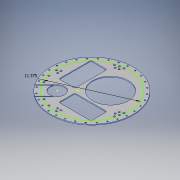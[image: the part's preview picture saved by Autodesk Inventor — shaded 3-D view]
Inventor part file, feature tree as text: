
AUTODESK INVENTOR PART (.ipt)
format: ipt  version: 2018 (Build 220112000, 112)  size: 325,120 bytes
history: native  units: in
note: dims shown in document units (in); Inventor stores cm internally (conversion verified against a paired STEP export)
features: sketch x8, extrude x4, hole x4, pattern_circular x1, fillet x1
ambient origin geometry x8: Origin, YZ Plane, XZ Plane, XY Plane, X Axis, Y Axis, Z Axis, Center Point
bodies: Solid1 (feature_tree)
feature tree (18):
  extrude  "Extrusion1"  TaperAngle=135.0deg  [1 undecoded]
  extrude  "Extrusion2"  Depth=2.25in
  hole  "Hole3"  [1 undecoded]
  pattern_circular  "Circular Pattern1"  [2 undecoded]
  hole  "Hole5"  [1 undecoded]
  hole  "Hole6"  [1 undecoded]
  extrude  "Extrusion3"  Depth=0.25in
  fillet  "Fillet1"  Radius=0.2749in
  sketch  "Sketch15"  dims[d8=12.75in]
  extrude  "Extrusion4"  Depth=0.25in
  hole  "Hole9"  [1 undecoded]
  sketch  "Sketch1"  dims[d0=3.6in d1=135.0deg]
  sketch  "Sketch2"  dims[d2=5.5in d3=2.25in]
  sketch  "Sketch6"  dims[d4=45.0deg d5=2.27in]
  sketch  "Sketch11"  dims[d6=1.56in]
  sketch  "Sketch13"  dims[d7=315.0deg]
  sketch  "Sketch17"  dims[d9=0.125in d10=0.0in]
  sketch  "Sketch19"  dims[d11=0.0in d12=0.0in d65=6.1in d66=0.0344in d67=0.196in d68=0.5in d69=0.375in d70=0.25in d71=0.5635in d72=0.75in d73=0.8108in d74=12.5984in d75=360.0deg d97=8.5in d98=0.2749in d99=8.5in d100=0.3436in d101=9.708in d102=9.708in d103=1.5748in d105=360.0deg d109=7.75in d110=0.962in d111=7.75in d112=0.8933in d116=0.266in d117=0.75in d118=0.507in d119=0.25in d120=0.5635in d121=1.0in d122=0.8108in d132=0.266in d133=0.75in d134=0.507in d135=0.25in d136=0.5635in d137=1.0in d138=0.8108in d147=11.0in d148=9.708in d149=9.708in d150=5.5in d152=5.5in d153=5.5in d154=5.5in d155=5.0in d156=90.0deg d157=2.5in d160=1.0in d161=45.0deg d162=1.0in d163=0.0in d164=2.9in d165=180.0deg d166=1.5in d167=90.0deg d168=0.25in d171=11.375in d180=0.1in d181=0.1in d182=1.0in d183=0.0in d201=10.1in d204=0.266in d205=0.75in d206=0.507in d207=0.25in d208=0.5635in d209=1.0in d210=0.8108in d212=1.0in d213=45.0deg d215=0.0206in d216=0.0206in]
note: 7 required parameter values undecoded (feature->parameter linkage not recoverable at this tier; creation-order binding heuristic only, values carry confidence <= 0.55)
